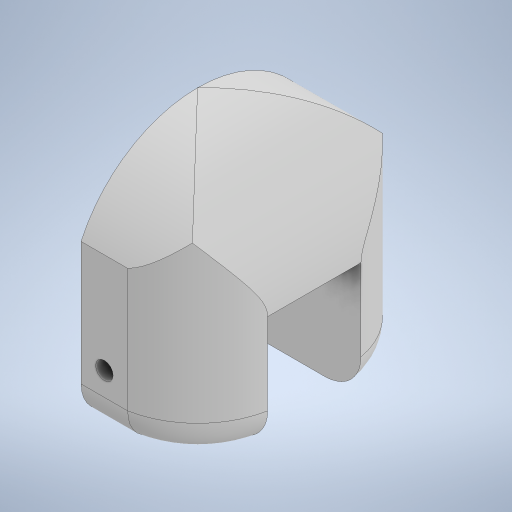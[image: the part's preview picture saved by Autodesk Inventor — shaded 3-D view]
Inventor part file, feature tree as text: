
AUTODESK INVENTOR PART (.ipt)
format: ipt  version: 2024.2 (Build 282272000, 272)  size: 332,800 bytes
history: native  units: mm
features: projected_geometry x5, extrude x4, sketch x4, other x1, fillet x1
ambient origin geometry x8: Origin, YZ Plane, XZ Plane, XY Plane, X Axis, Y Axis, Z Axis, Center Point
bodies: Body1 (feature_tree)
feature tree (15):
  other  "Bryła1"
  extrude  "Wyciągnięcie proste1"  Depth=13.0mm
  extrude  "Wyciągnięcie proste5"  Depth=11.0mm
  extrude  "Wyciągnięcie proste6"  Depth=10.0mm TaperAngle=0.0deg
  fillet  "Zaokrąglenie2"  Radius=10.0mm
  extrude  "Wyciągnięcie proste7"  Depth=8.0mm
  sketch  "Szkic1"
  sketch  "Szkic5"
  projected_geometry  "Pętla rzutowana5"
  projected_geometry  "Pętla rzutowana6"
  projected_geometry  "Pętla rzutowana7"
  sketch  "Szkic6"
  sketch  "Szkic7"
  projected_geometry  "Pętla rzutowana8"
  projected_geometry  "Pętla rzutowana9"
